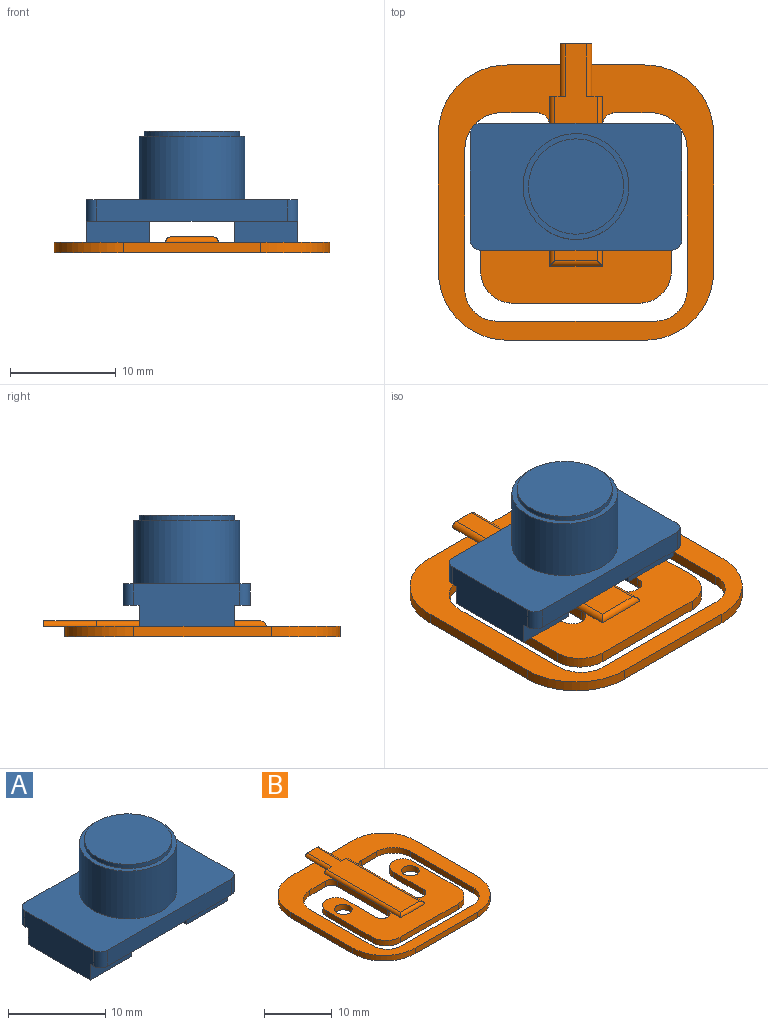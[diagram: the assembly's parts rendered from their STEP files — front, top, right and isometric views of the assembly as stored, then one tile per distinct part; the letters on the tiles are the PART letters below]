
ASSEMBLY  parts=2 mates=1
PART A: 26 faces, bbox 20x12x10.5 mm
  f0: plane 6x2mm, normal (0,-1,0), area 12mm2, adj f1,f3,f5,f7
  f1: plane 9x2mm, normal (1,0,0), area 18mm2, adj f0,f2,f5,f7
  f2: plane 6x2mm, normal (0,1,0), area 12mm2, adj f1,f3,f5,f7
  f3: plane 10x4mm, normal (-1,0,0), area 38mm2, adj f0,f2,f5,f7,f17,f22,f24
  f4: cylinder r=1.3mm len=2.6mm, axis (0,0,-1), area 16.3mm2, adj f5,f6
  f5: plane 9x6mm, normal (0,0,-1), area 48.7mm2, adj f0,f1,f2,f3,f4
  f6: plane 2.6x2.6mm, normal (0,0,-1), area 5.3mm2, adj f4
  f7: plane 20x12mm, normal (0,0,-1), area 131.1mm2, adj f0,f1,f2,f3,f8,f9,f10,f11
  f8: plane 6x2mm, normal (0,-1,0), area 12mm2, adj f7,f9,f11,f13
  f9: plane 10x4mm, normal (1,0,0), area 38mm2, adj f7,f8,f10,f13,f17,f23,f25
  f10: plane 6x2mm, normal (0,1,0), area 12mm2, adj f7,f9,f11,f13
  f11: plane 9x2mm, normal (-1,0,0), area 18mm2, adj f7,f8,f10,f13
  f12: cylinder r=1.3mm len=2.6mm, axis (0,0,-1), area 16.3mm2, adj f13,f14
  f13: plane 9x6mm, normal (0,0,-1), area 48.7mm2, adj f8,f9,f10,f11,f12
  f14: plane 2.6x2.6mm, normal (0,0,-1), area 5.3mm2, adj f12
  f15: plane 18x2mm, normal (0,-1,0), area 36mm2, adj f7,f17,f22,f23
  f16: plane 18x2mm, normal (0,1,0), area 36mm2, adj f7,f17,f24,f25
  f17: plane 20x12mm, normal (0,0,1), area 160.6mm2, adj f3,f9,f15,f16,f18,f22,f23,f24
  f18: cylinder r=5mm len=10mm, axis (0,0,-1), area 188.5mm2, adj f17,f19
  f19: plane 10x10mm, normal (0,0,1), area 14.9mm2, adj f18,f20
  f20: cylinder r=4.5mm len=9mm, axis (0,0,-1), area 14.1mm2, adj f19,f21
  f21: plane 9x9mm, normal (0,0,1), area 63.6mm2, adj f20
  f22: cylinder r=1mm len=2mm, axis (0,0,-1), area 3.1mm2, adj f3,f7,f15,f17
  f23: cylinder r=1mm len=2mm, axis (0,0,-1), area 3.1mm2, adj f7,f9,f15,f17
  f24: cylinder r=1mm len=2mm, axis (0,0,1), area 3.1mm2, adj f3,f7,f16,f17
  f25: cylinder r=1mm len=2mm, axis (0,0,1), area 3.1mm2, adj f7,f9,f16,f17
PART B: 47 faces, bbox 26x28x1.5 mm
  f0: plane 26x26mm, normal (0,0,1), area 219.3mm2, adj f1,f2,f3,f4,f5,f6,f7,f20
  f1: plane 13x1mm, normal (1,0,0), area 13mm2, adj f0,f2,f34,f36
  f2: cylinder r=6.5mm len=6.5mm, axis (0,0,-1), area 10.2mm2, adj f0,f1,f3,f36
  f3: plane 13x1mm, normal (0,1,0), area 13mm2, adj f0,f2,f4,f36,f37
  f4: cylinder r=6.5mm len=6.5mm, axis (0,0,-1), area 10.2mm2, adj f0,f3,f5,f36
  f5: plane 13x1mm, normal (-1,0,0), area 13mm2, adj f0,f4,f6,f36
  f6: cylinder r=6.5mm len=6.5mm, axis (0,0,-1), area 10.2mm2, adj f0,f5,f7,f36
  f7: plane 13x1mm, normal (0,-1,0), area 13mm2, adj f0,f6,f34,f36
  f8: cylinder r=1.25mm len=2.5mm, axis (0,0,-1), area 3.9mm2, adj f9,f33,f35,f36
  f9: plane 6.25x1mm, normal (1,0,0), area 6.2mm2, adj f8,f10,f35,f36
  f10: cylinder r=2mm len=4mm, axis (0,0,-1), area 6.3mm2, adj f9,f11,f35,f36
  f11: plane 9.5x1mm, normal (-1,0,0), area 9.5mm2, adj f10,f12,f35,f36
  f12: cylinder r=3mm len=3mm, axis (0,0,-1), area 4.7mm2, adj f11,f13,f35,f36
  f13: plane 12x1mm, normal (0,-1,0), area 12mm2, adj f12,f14,f35,f36
  f14: cylinder r=3mm len=3mm, axis (0,0,-1), area 4.7mm2, adj f13,f15,f35,f36
  f15: plane 9.5x1mm, normal (1,0,0), area 9.5mm2, adj f14,f16,f35,f36
  f16: cylinder r=2mm len=4mm, axis (0,0,-1), area 6.3mm2, adj f15,f17,f35,f36
  f17: plane 6.25x1mm, normal (-1,0,0), area 6.2mm2, adj f16,f18,f35,f36
  f18: cylinder r=1.25mm len=2.5mm, axis (0,0,-1), area 3.9mm2, adj f17,f19,f35,f36
  f19: plane 10.5x1mm, normal (1,0,0), area 10.5mm2, adj f18,f20,f36,f42
  f20: cylinder r=1.25mm len=1.25mm, axis (0,0,-1), area 2mm2, adj f0,f19,f21,f36
  f21: plane 3.25x1mm, normal (0,-1,0), area 3.2mm2, adj f0,f20,f22,f36
  f22: cylinder r=3.5mm len=3.5mm, axis (0,0,-1), area 5.5mm2, adj f0,f21,f23,f36
  f23: plane 13.2x1mm, normal (-1,0,0), area 13.2mm2, adj f0,f22,f24,f36
  f24: cylinder r=3mm len=3mm, axis (0,0,-1), area 4.7mm2, adj f0,f23,f25,f36
  f25: plane 15x1mm, normal (0,1,0), area 15mm2, adj f0,f24,f26,f36
  f26: cylinder r=3mm len=3mm, axis (0,0,-1), area 4.7mm2, adj f0,f25,f27,f36
  f27: plane 13.2x1mm, normal (1,0,0), area 13.2mm2, adj f0,f26,f28,f36
  f28: cylinder r=3.5mm len=3.5mm, axis (0,0,-1), area 5.5mm2, adj f0,f27,f29,f36
  f29: plane 3.25x1mm, normal (0,-1,0), area 3.2mm2, adj f0,f28,f30,f36
  f30: cylinder r=1.25mm len=1.25mm, axis (0,0,-1), area 2mm2, adj f0,f29,f33,f36
  f31: cylinder r=1.3mm len=2.6mm, axis (0,0,-1), area 8.2mm2, adj f35,f36
  f32: cylinder r=1.3mm len=2.6mm, axis (0,0,-1), area 8.2mm2, adj f35,f36
  f33: plane 10.5x1mm, normal (-1,0,0), area 10.5mm2, adj f8,f30,f36,f44
  f34: cylinder r=6.5mm len=6.5mm, axis (0,0,-1), area 10.2mm2, adj f0,f1,f7,f36
  f35: plane 18x14.5mm, normal (0,0,1), area 141.9mm2, adj f8,f9,f10,f11,f12,f13,f14,f15
  f36: plane 26x26mm, normal (0,0,-1), area 450.2mm2, adj f1,f2,f3,f4,f5,f6,f7,f8
  f37: plane 3x2mm, normal (0,0,-1), area 6mm2, adj f3,f40,f45,f46
  f38: plane 1.5x0.5mm, normal (0,1,0), area 0.5mm2, adj f0,f41,f44,f45
  f39: plane 1.5x0.5mm, normal (0,1,0), area 0.5mm2, adj f0,f41,f42,f46
  f40: plane 3x0.5mm, normal (0,1,0), area 1.4mm2, adj f37,f41,f45,f46
  f41: plane 20.5x4mm, normal (0,0,1), area 72mm2, adj f38,f39,f40,f42,f43,f44,f45,f46
  f42: cylinder r=0.5mm len=16mm, axis (0,-1,0), area 12.4mm2, adj f0,f19,f35,f39,f41,f43
  f43: cylinder r=0.5mm len=5mm, axis (-1,0,0), area 3.6mm2, adj f35,f41,f42,f44
  f44: cylinder r=0.5mm len=16mm, axis (0,-1,0), area 12.4mm2, adj f0,f33,f35,f38,f41,f43
  f45: cylinder r=0.5mm len=5mm, axis (0,1,0), area 3.9mm2, adj f0,f37,f38,f40,f41
  f46: cylinder r=0.5mm len=5mm, axis (0,-1,0), area 3.9mm2, adj f0,f37,f39,f40,f41
PLACE A at identity
PLACE B at identity fixed
MATE fastened A.f4 <-> B.f31  axis (0,0,-1) through (6,14.5,1)mm
